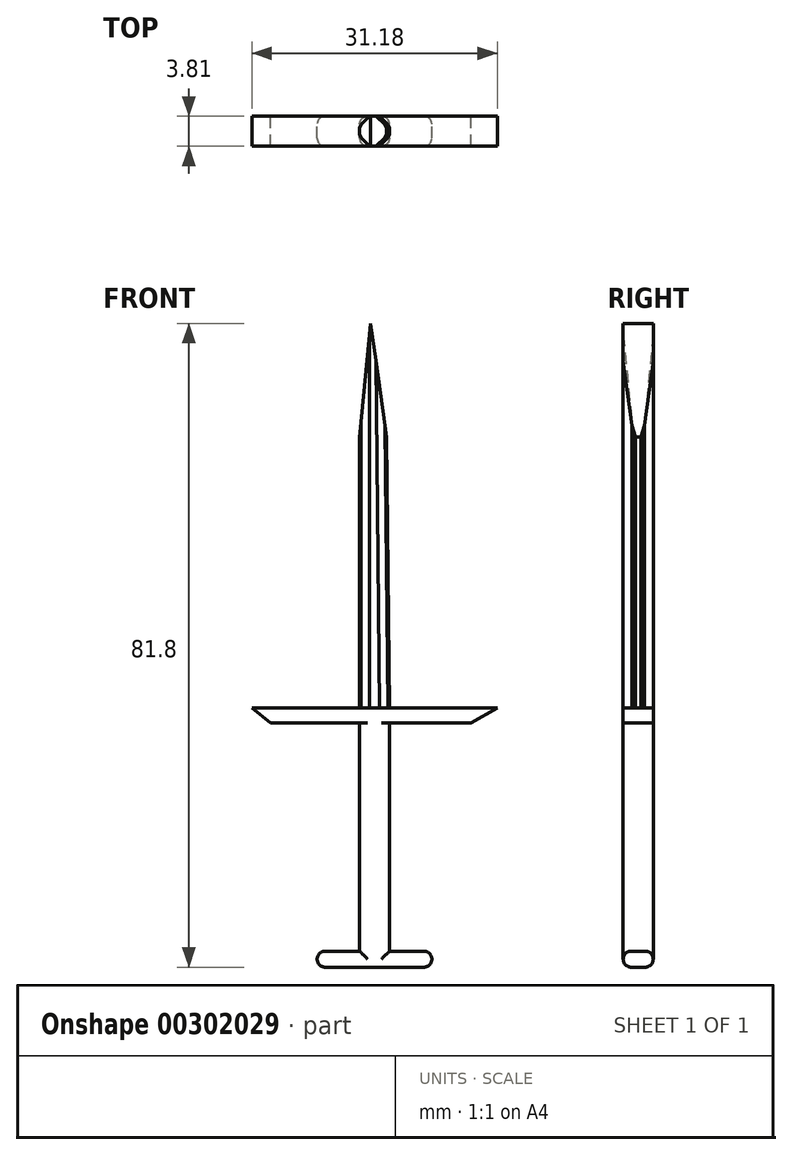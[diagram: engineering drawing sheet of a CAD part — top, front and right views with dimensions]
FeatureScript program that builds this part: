
annotation { "Feature Type Name" : "Feature", "Feature Type Description" : "" }
export const myFeature = defineFeature(function(context is Context, id is Id, definition is map)
    precondition{}
    {
        {
            var Q0;
            Q0=qCreatedBy(makeId("Front.planeOp"),FACE);
            var sketch = newSketch(context, id + "F0", { "sketchPlane" : qUnion([Q0])});
            skLineSegment(sketch, "E0", {"start": v(-36.77, -27.56) * mm, "end": v(-36.77, -56.58) * mm});
            skLineSegment(sketch, "E1", {"start": v(-36.77, -56.58) * mm, "end": v(-42.16, -56.58) * mm});
            skLineSegment(sketch, "E2", {"start": v(-42.16, -56.58) * mm, "end": v(-42.16, -58.62) * mm});
            skLineSegment(sketch, "E3", {"start": v(-42.16, -58.62) * mm, "end": v(-27.6, -58.62) * mm});
            skLineSegment(sketch, "E4", {"start": v(-27.6, -58.62) * mm, "end": v(-27.6, -56.58) * mm});
            skLineSegment(sketch, "E5", {"start": v(-27.6, -56.58) * mm, "end": v(-32.99, -56.58) * mm});
            skLineSegment(sketch, "E6", {"start": v(-32.99, -56.58) * mm, "end": v(-32.99, -27.56) * mm});
            skLineSegment(sketch, "E7", {"start": v(-32.99, -27.56) * mm, "end": v(-36.55, -27.56) * mm});
            skLineSegment(sketch, "E8", {"start": v(-36.77, -27.56) * mm, "end": v(-48.1, -27.56) * mm});
            skLineSegment(sketch, "E9", {"start": v(-48.1, -27.56) * mm, "end": v(-50.47, -25.7) * mm});
            skLineSegment(sketch, "E10", {"start": v(-50.47, -25.7) * mm, "end": v(-36.77, -25.7) * mm});
            skLineSegment(sketch, "E11", {"start": v(-36.77, -25.7) * mm, "end": v(-32.99, -25.7) * mm});
            skLineSegment(sketch, "E12", {"start": v(-32.99, -25.7) * mm, "end": v(-19.3, -25.7) * mm});
            skLineSegment(sketch, "E13", {"start": v(-19.3, -25.7) * mm, "end": v(-22.64, -27.56) * mm});
            skLineSegment(sketch, "E14", {"start": v(-22.64, -27.56) * mm, "end": v(-32.99, -27.56) * mm});
            skLineSegment(sketch, "E15", {"start": v(-36.77, -25.7) * mm, "end": v(-36.77, 8.76) * mm});
            skLineSegment(sketch, "E16", {"start": v(-36.77, 8.76) * mm, "end": v(-35.36, 23.18) * mm});
            skLineSegment(sketch, "E17", {"start": v(-35.36, 23.18) * mm, "end": v(-33.33, 8.76) * mm});
            skLineSegment(sketch, "E18", {"start": v(-33.33, 8.76) * mm, "end": v(-32.99, -25.7) * mm});
            skSolve(sketch);
        }
        {
            var Q0;
            Q0=makeQuery(id+"F0.imprint","IMPRINT",FACE,{"disambiguationData":[TD([[makeQuery(id+"F0.imprint","IMPRINT",EDGE,{"derivedFrom":sQuery(id+"F0.wireOp",EDGE,"E0")}),1.0]])]});
            extrude(context, id + "F1", {"entities" : qUnion([Q0]), "depth" : 3.8 * mm});
        }
        {
            var Q0;
            Q0=makeQuery(id+"F0.imprint","IMPRINT",FACE,{"disambiguationData":[TD([[makeQuery(id+"F0.imprint","IMPRINT",EDGE,{"derivedFrom":sQuery(id+"F0.wireOp",EDGE,"E11")}),1.0]])]});
            extrude(context, id + "F2", {"entities" : qUnion([Q0]), "depth" : 3.8 * mm});
        }
        {
            var Q0;
            Q0=makeQuery(id+"F2.opExtrude","CAP_EDGE",EDGE,{"disambiguationData":[OSD([sQuery(id+"F0.wireOp",EDGE,"E18")])],"isStart":true});
            var Q1;
            Q1=makeQuery(id+"F2.opExtrude","CAP_EDGE",EDGE,{"disambiguationData":[OSD([sQuery(id+"F0.wireOp",EDGE,"E15")])],"isStart":true});
            var Q2;
            Q2=makeQuery(id+"F2.opExtrude","CAP_EDGE",EDGE,{"disambiguationData":[OSD([sQuery(id+"F0.wireOp",EDGE,"E15")])],"isStart":false});
            var Q3;
            Q3=makeQuery(id+"F2.opExtrude","CAP_EDGE",EDGE,{"disambiguationData":[OSD([sQuery(id+"F0.wireOp",EDGE,"E18")])],"isStart":false});
            chamfer(context, id + "F3", {"entities" : qUnion([Q0, Q1, Q2, Q3]), "width" : 1.27 * mm, "tangentPropagation" : true});
        }
        {
            var Q0;
            {var subQ0=sQuery(id+"F0.wireOp",EDGE,"E18");Q0=makeQuery(id+"F3.opChamfer","BLEND_EDGE",EDGE,{"blendedFrom":[makeQuery(id+"F2.opExtrude","CAP_EDGE",EDGE,{"disambiguationData":[OSD([subQ0])],"isStart":true}),makeQuery(id+"F2.opExtrude","SWEPT_FACE",FACE,{"disambiguationData":[OSD([subQ0])]})],"blendedInto":[makeQuery(id+"F2.opExtrude","SWEPT_FACE",FACE,{"disambiguationData":[OSD([subQ0])]})]});}
            var Q1;
            {var subQ0=sQuery(id+"F0.wireOp",EDGE,"E18");Q1=makeQuery(id+"F3.opChamfer","BLEND_EDGE",EDGE,{"blendedFrom":[makeQuery(id+"F2.opExtrude","CAP_EDGE",EDGE,{"disambiguationData":[OSD([subQ0])],"isStart":false}),makeQuery(id+"F2.opExtrude","SWEPT_FACE",FACE,{"disambiguationData":[OSD([subQ0])]})],"blendedInto":[makeQuery(id+"F2.opExtrude","SWEPT_FACE",FACE,{"disambiguationData":[OSD([subQ0])]})]});}
            var Q2;
            {var subQ0=sQuery(id+"F0.wireOp",EDGE,"E15");Q2=makeQuery(id+"F3.opChamfer","BLEND_EDGE",EDGE,{"blendedFrom":[makeQuery(id+"F2.opExtrude","CAP_EDGE",EDGE,{"disambiguationData":[OSD([subQ0])],"isStart":true}),makeQuery(id+"F2.opExtrude","SWEPT_FACE",FACE,{"disambiguationData":[OSD([subQ0])]})],"blendedInto":[makeQuery(id+"F2.opExtrude","SWEPT_FACE",FACE,{"disambiguationData":[OSD([subQ0])]})]});}
            var Q3;
            {var subQ0=sQuery(id+"F0.wireOp",EDGE,"E15");Q3=makeQuery(id+"F3.opChamfer","BLEND_EDGE",EDGE,{"blendedFrom":[makeQuery(id+"F2.opExtrude","CAP_EDGE",EDGE,{"disambiguationData":[OSD([subQ0])],"isStart":false}),makeQuery(id+"F2.opExtrude","SWEPT_FACE",FACE,{"disambiguationData":[OSD([subQ0])]})],"blendedInto":[makeQuery(id+"F2.opExtrude","SWEPT_FACE",FACE,{"disambiguationData":[OSD([subQ0])]})]});}
            chamfer(context, id + "F4", {"entities" : qUnion([Q0, Q1, Q2, Q3]), "width" : 0.64 * mm, "tangentPropagation" : true});
        }
        {
            var Q0;
            Q0=makeQuery(id+"F1.opExtrude","CAP_EDGE",EDGE,{"disambiguationData":[OSD([sQuery(id+"F0.wireOp",EDGE,"E6")])],"isStart":true});
            var Q1;
            Q1=makeQuery(id+"F1.opExtrude","CAP_EDGE",EDGE,{"disambiguationData":[OSD([sQuery(id+"F0.wireOp",EDGE,"E0")])],"isStart":true});
            var Q2;
            Q2=makeQuery(id+"F1.opExtrude","CAP_EDGE",EDGE,{"disambiguationData":[OSD([sQuery(id+"F0.wireOp",EDGE,"E0")])],"isStart":false});
            var Q3;
            Q3=makeQuery(id+"F1.opExtrude","CAP_EDGE",EDGE,{"disambiguationData":[OSD([sQuery(id+"F0.wireOp",EDGE,"E6")])],"isStart":false});
            var Q4;
            Q4=makeQuery(id+"F1.opExtrude","CAP_EDGE",EDGE,{"disambiguationData":[OSD([sQuery(id+"F0.wireOp",EDGE,"E3")])],"isStart":false});
            var Q5;
            Q5=makeQuery(id+"F1.opExtrude","CAP_EDGE",EDGE,{"disambiguationData":[OSD([sQuery(id+"F0.wireOp",EDGE,"E2")])],"isStart":false});
            var Q6;
            Q6=makeQuery(id+"F1.opExtrude","CAP_EDGE",EDGE,{"disambiguationData":[OSD([sQuery(id+"F0.wireOp",EDGE,"E5")])],"isStart":false});
            var Q7;
            Q7=makeQuery(id+"F1.opExtrude","CAP_EDGE",EDGE,{"disambiguationData":[OSD([sQuery(id+"F0.wireOp",EDGE,"E1")])],"isStart":false});
            var Q8;
            Q8=makeQuery(id+"F1.opExtrude","SWEPT_EDGE",EDGE,{"disambiguationData":[OSD([sQuery(id+"F0.wireOp",EDGE,"E4"),sQuery(id+"F0.wireOp",EDGE,"E5")])]});
            var Q9;
            Q9=makeQuery(id+"F1.opExtrude","SWEPT_EDGE",EDGE,{"disambiguationData":[OSD([sQuery(id+"F0.wireOp",EDGE,"E3"),sQuery(id+"F0.wireOp",EDGE,"E4")])]});
            var Q10;
            Q10=makeQuery(id+"F1.opExtrude","CAP_EDGE",EDGE,{"disambiguationData":[OSD([sQuery(id+"F0.wireOp",EDGE,"E5")])],"isStart":true});
            var Q11;
            Q11=makeQuery(id+"F1.opExtrude","CAP_EDGE",EDGE,{"disambiguationData":[OSD([sQuery(id+"F0.wireOp",EDGE,"E1")])],"isStart":true});
            var Q12;
            Q12=makeQuery(id+"F1.opExtrude","CAP_EDGE",EDGE,{"disambiguationData":[OSD([sQuery(id+"F0.wireOp",EDGE,"E2")])],"isStart":true});
            var Q13;
            Q13=makeQuery(id+"F1.opExtrude","SWEPT_EDGE",EDGE,{"disambiguationData":[OSD([sQuery(id+"F0.wireOp",EDGE,"E2"),sQuery(id+"F0.wireOp",EDGE,"E3")])]});
            var Q14;
            Q14=makeQuery(id+"F1.opExtrude","CAP_EDGE",EDGE,{"disambiguationData":[OSD([sQuery(id+"F0.wireOp",EDGE,"E4")])],"isStart":true});
            var Q15;
            Q15=makeQuery(id+"F1.opExtrude","CAP_EDGE",EDGE,{"disambiguationData":[OSD([sQuery(id+"F0.wireOp",EDGE,"E4")])],"isStart":false});
            var Q16;
            Q16=makeQuery(id+"F1.opExtrude","SWEPT_EDGE",EDGE,{"disambiguationData":[OSD([sQuery(id+"F0.wireOp",EDGE,"E1"),sQuery(id+"F0.wireOp",EDGE,"E2")])]});
            var Q17;
            Q17=makeQuery(id+"F1.opExtrude","CAP_EDGE",EDGE,{"disambiguationData":[OSD([sQuery(id+"F0.wireOp",EDGE,"E3")])],"isStart":true});
            fillet(context, id + "F5", {"entities" : qUnion([Q0, Q1, Q2, Q3, Q4, Q5, Q6, Q7, Q8, Q9, Q10, Q11, Q12, Q13, Q14, Q15, Q16, Q17]), "radius" : 1.02 * mm, "tangentPropagation" : true, "allowEdgeOverflow" : false});
        }
    });
